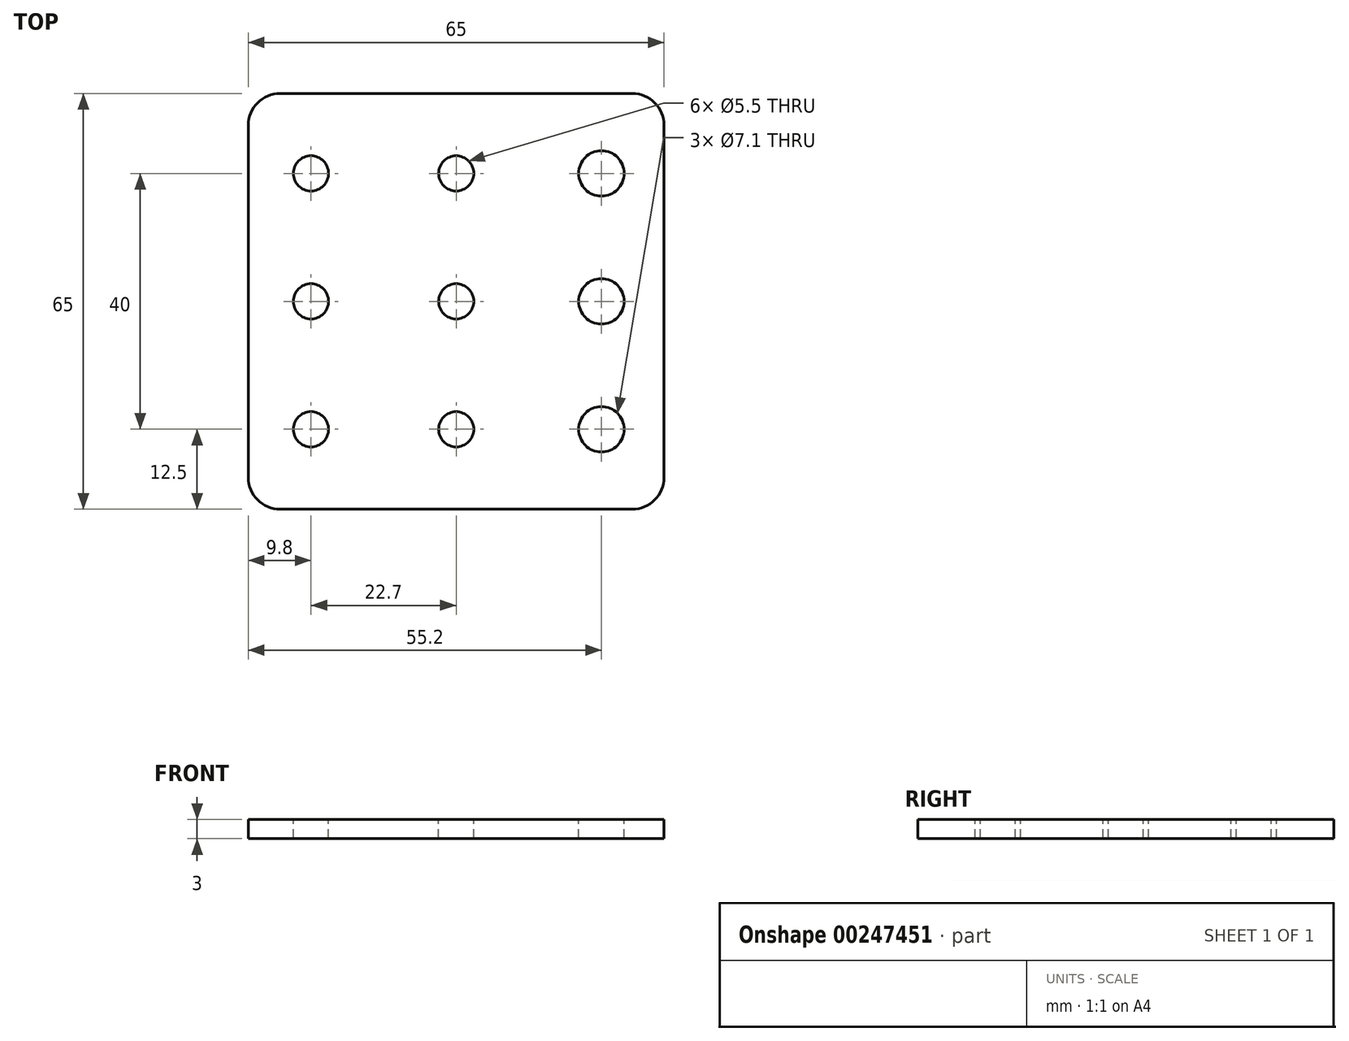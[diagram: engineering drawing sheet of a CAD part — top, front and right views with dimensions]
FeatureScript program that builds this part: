
annotation { "Feature Type Name" : "Feature", "Feature Type Description" : "" }
export const myFeature = defineFeature(function(context is Context, id is Id, definition is map)
    precondition{}
    {
        {
            var Q0;
            Q0=qCreatedBy(makeId("Top.planeOp"),FACE);
            var sketch = newSketch(context, id + "F0", { "sketchPlane" : qUnion([Q0])});
            skLineSegment(sketch, "E0.bottom", {"start": v(-32.5, -32.5) * mm, "end": v(32.5, -32.5) * mm});
            skLineSegment(sketch, "E0.top", {"start": v(-32.5, 32.5) * mm, "end": v(32.5, 32.5) * mm});
            skLineSegment(sketch, "E0.left", {"start": v(-32.5, -32.5) * mm, "end": v(-32.5, 32.5) * mm});
            skLineSegment(sketch, "E0.right", {"start": v(32.5, -32.5) * mm, "end": v(32.5, 32.5) * mm});
            skPoint(sketch, "E0.middle", {"position": v(0, 0) * mm});
            skSolve(sketch);
        }
        {
            var Q0;
            Q0=makeQuery(id+"F0.imprint","IMPRINT",FACE,{"disambiguationData":[TD([[makeQuery(id+"F0.imprint","IMPRINT",EDGE,{"derivedFrom":sQuery(id+"F0.wireOp",EDGE,"E0.bottom")}),1.0]])]});
            extrude(context, id + "F1", {"entities" : qUnion([Q0]), "depth" : 3 * mm});
        }
        {
            var Q0;
            Q0=makeQuery(id+"F1.opExtrude","SWEPT_EDGE",EDGE,{"disambiguationData":[OSD([sQuery(id+"F0.wireOp",EDGE,"E0.top"),sQuery(id+"F0.wireOp",EDGE,"E0.left")])]});
            var Q1;
            Q1=makeQuery(id+"F1.opExtrude","SWEPT_EDGE",EDGE,{"disambiguationData":[OSD([sQuery(id+"F0.wireOp",EDGE,"E0.top"),sQuery(id+"F0.wireOp",EDGE,"E0.right")])]});
            var Q2;
            Q2=makeQuery(id+"F1.opExtrude","SWEPT_EDGE",EDGE,{"disambiguationData":[OSD([sQuery(id+"F0.wireOp",EDGE,"E0.bottom"),sQuery(id+"F0.wireOp",EDGE,"E0.right")])]});
            var Q3;
            Q3=makeQuery(id+"F1.opExtrude","SWEPT_EDGE",EDGE,{"disambiguationData":[OSD([sQuery(id+"F0.wireOp",EDGE,"E0.bottom"),sQuery(id+"F0.wireOp",EDGE,"E0.left")])]});
            fillet(context, id + "F2", {"entities" : qUnion([Q0, Q1, Q2, Q3]), "radius" : 5 * mm, "tangentPropagation" : true, "allowEdgeOverflow" : false});
        }
        {
            var Q0;
            Q0=makeQuery(id+"F1.opExtrude","CAP_FACE",FACE,{"disambiguationData":[OSD([sQuery(id+"F0.wireOp",EDGE,"E0.bottom"),sQuery(id+"F0.wireOp",EDGE,"E0.top"),sQuery(id+"F0.wireOp",EDGE,"E0.left"),sQuery(id+"F0.wireOp",EDGE,"E0.right")])],"isStart":false});
            var sketch = newSketch(context, id + "F3", { "sketchPlane" : qUnion([Q0])});
            skPoint(sketch, "E1", {"position": v(0, 20) * mm});
            skPoint(sketch, "E2", {"position": v(-22.7, 20) * mm});
            skLineSegment(sketch, "E3", {"start": v(-22.7, 0) * mm, "end": v(24.73, 0) * mm});
            skPoint(sketch, "E4.MirrorP", {"position": v(-22.7, -20) * mm});
            skPoint(sketch, "E5.MirrorP", {"position": v(0, -20) * mm});
            skPoint(sketch, "E6", {"position": v(-22.7, 0) * mm});
            skPoint(sketch, "E7", {"position": v(0, 0) * mm});
            skSolve(sketch);
        }
        {
            var Q0;
            Q0=sQuery(id+"F3.wireOp",VERTEX,"E2");
            var Q1;
            Q1=sQuery(id+"F3.wireOp",VERTEX,"E4.MirrorP");
            var Q2;
            Q2=sQuery(id+"F3.wireOp",VERTEX,"E5.MirrorP");
            var Q3;
            Q3=sQuery(id+"F3.wireOp",VERTEX,"E1");
            var Q4;
            Q4=sQuery(id+"F3.wireOp",VERTEX,"E6");
            var Q5;
            Q5=sQuery(id+"F3.wireOp",VERTEX,"E7");
            var Q6;
            Q6=makeQuery(id+"F1.opExtrude","SWEPT_BODY",BODY,{"disambiguationData":[OSD([sQuery(id+"F0.wireOp",EDGE,"E0.bottom"),sQuery(id+"F0.wireOp",EDGE,"E0.top"),sQuery(id+"F0.wireOp",EDGE,"E0.left"),sQuery(id+"F0.wireOp",EDGE,"E0.right")])]});
            hole(context, id + "F4", {"style" : HoleStyle.SIMPLE, "endStyle" : HoleEndStyle.THROUGH, "standardTappedOrClearance" : lookupTablePath({ "standard" : "ISO", "fit" : "Normal", "size" : "M5", "type" : "Clearance" }), "standardBlindInLast" : lookupTablePath({ "fit" : "Standard", "standard" : "ISO", "size" : "M5", "type" : "Clearance" }), "holeDiameter" : 5.5 * mm, "tappedDepth" : 12 * mm, "tapClearance" : 3, "locations" : qUnion([Q0, Q1, Q2, Q3, Q4, Q5]), "scope" : qUnion([Q6])});
        }
        {
            var Q0;
            Q0=makeQuery(id+"F1.opExtrude","CAP_FACE",FACE,{"disambiguationData":[OSD([sQuery(id+"F0.wireOp",EDGE,"E0.bottom"),sQuery(id+"F0.wireOp",EDGE,"E0.top"),sQuery(id+"F0.wireOp",EDGE,"E0.left"),sQuery(id+"F0.wireOp",EDGE,"E0.right")])],"isStart":false});
            var sketch = newSketch(context, id + "F5", { "sketchPlane" : qUnion([Q0])});
            skPoint(sketch, "E8", {"position": v(22.7, 20) * mm});
            skLineSegment(sketch, "E9", {"start": v(26.22, 0) * mm, "end": v(0, 0) * mm});
            skPoint(sketch, "E10.MirrorP", {"position": v(22.7, -20) * mm});
            skPoint(sketch, "E11", {"position": v(-22.7, 20) * mm});
            skPoint(sketch, "E12", {"position": v(22.7, 0) * mm});
            skSolve(sketch);
        }
        {
            var Q0;
            Q0=sQuery(id+"F5.wireOp",VERTEX,"E8");
            var Q1;
            Q1=sQuery(id+"F5.wireOp",VERTEX,"E10.MirrorP");
            var Q2;
            Q2=sQuery(id+"F5.wireOp",VERTEX,"E12");
            var Q3;
            Q3=makeQuery(id+"F1.opExtrude","SWEPT_BODY",BODY,{"disambiguationData":[OSD([sQuery(id+"F0.wireOp",EDGE,"E0.bottom"),sQuery(id+"F0.wireOp",EDGE,"E0.top"),sQuery(id+"F0.wireOp",EDGE,"E0.left"),sQuery(id+"F0.wireOp",EDGE,"E0.right")])]});
            hole(context, id + "F6", {"style" : HoleStyle.SIMPLE, "endStyle" : HoleEndStyle.THROUGH, "holeDiameter" : 7.1 * mm, "tappedDepth" : 12 * mm, "tapClearance" : 3, "locations" : qUnion([Q0, Q1, Q2]), "scope" : qUnion([Q3])});
        }
    });
